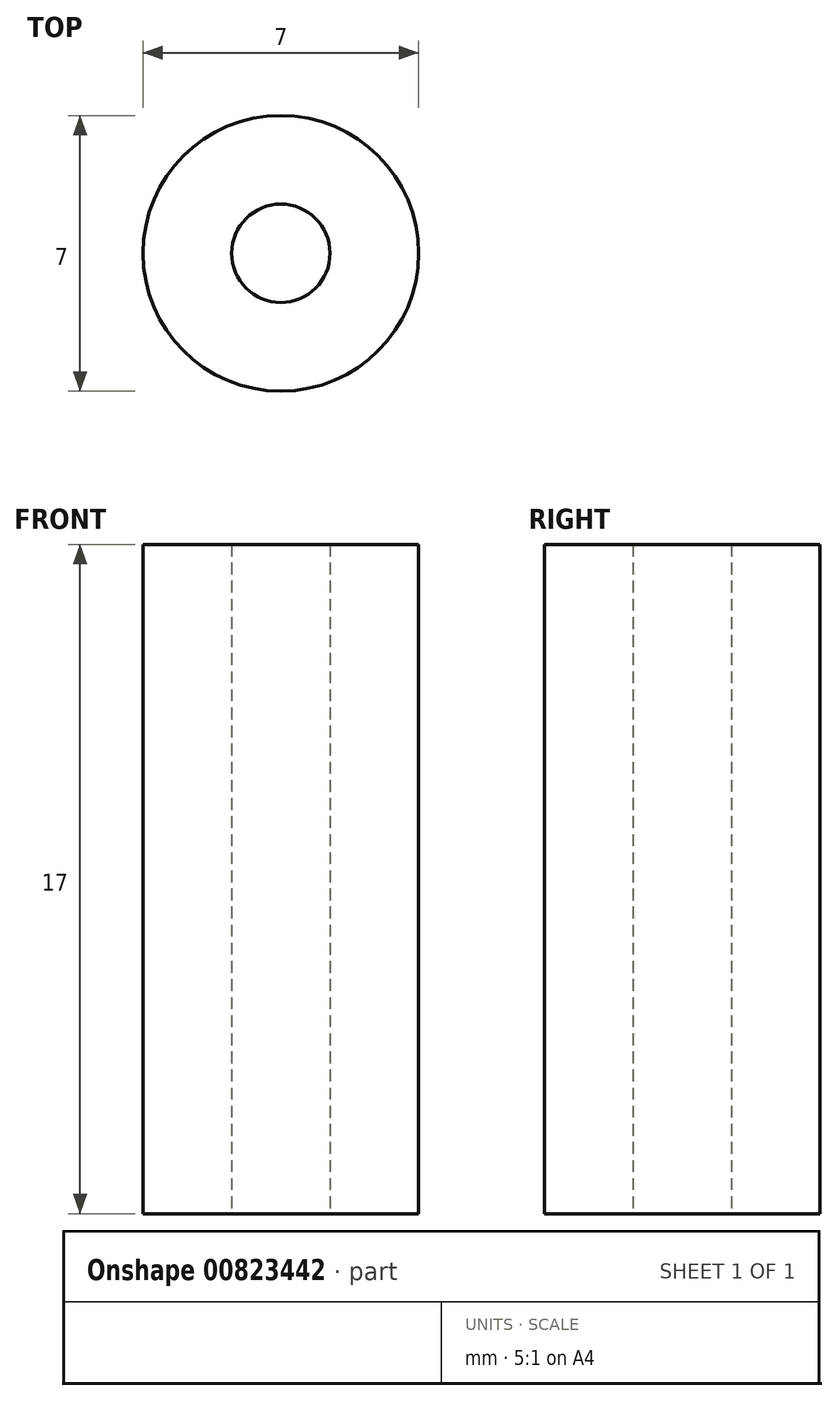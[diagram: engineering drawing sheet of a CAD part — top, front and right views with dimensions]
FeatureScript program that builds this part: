
annotation { "Feature Type Name" : "Feature", "Feature Type Description" : "" }
export const myFeature = defineFeature(function(context is Context, id is Id, definition is map)
    precondition{}
    {
        {
            var Q0;
            Q0=qCreatedBy(makeId("Top.planeOp"),FACE);
            var sketch = newSketch(context, id + "F0", { "sketchPlane" : qUnion([Q0])});
            skCircle(sketch, "E0", {"center": v(0, 0) * mm, "radius": 1.25 * mm});
            skCircle(sketch, "E1", {"center": v(0, 0) * mm, "radius": 3.5 * mm});
            skSolve(sketch);
        }
        {
            var Q0;
            Q0 = qSketchRegion(id + "F0", true);
            extrude(context, id + "F1", {"entities" : qUnion([Q0]), "depth" : 17 * mm, "offsetDistance" : 25 * mm});
        }
    });
